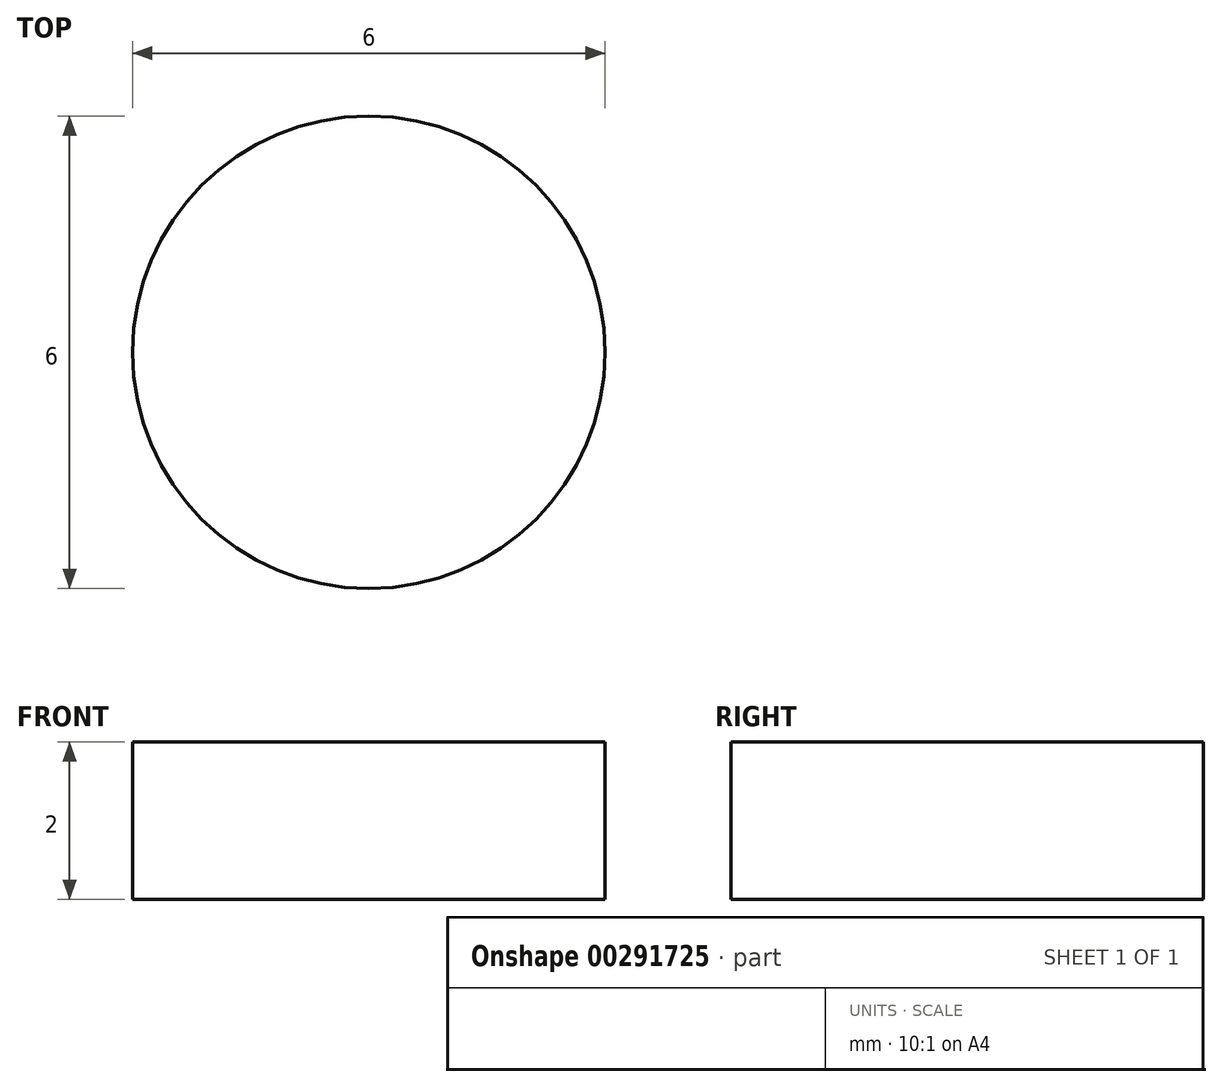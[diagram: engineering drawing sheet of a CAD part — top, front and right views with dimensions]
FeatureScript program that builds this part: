
annotation { "Feature Type Name" : "Feature", "Feature Type Description" : "" }
export const myFeature = defineFeature(function(context is Context, id is Id, definition is map)
    precondition{}
    {
        {
            var Q0;
            Q0=qCreatedBy(makeId("Top.planeOp"),FACE);
            var sketch = newSketch(context, id + "F0", { "sketchPlane" : qUnion([Q0])});
            skCircle(sketch, "E0", {"center": v(0, 0) * mm, "radius": 3 * mm});
            skSolve(sketch);
        }
        {
            var Q0;
            Q0 = qSketchRegion(id + "F0", true);
            extrude(context, id + "F1", {"entities" : qUnion([Q0]), "depth" : 2 * mm});
        }
    });
